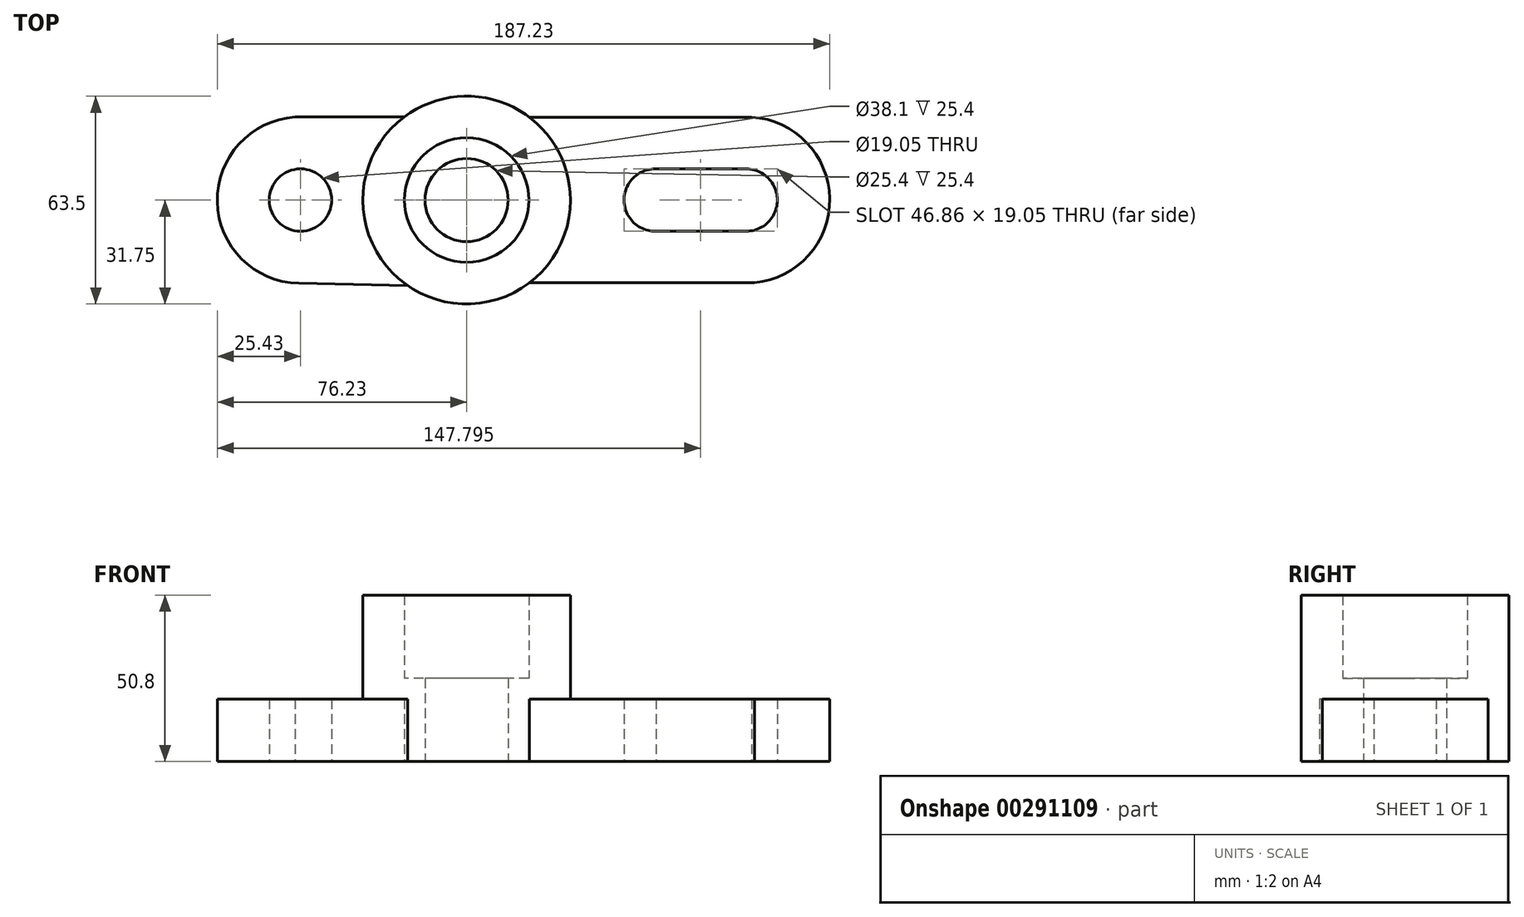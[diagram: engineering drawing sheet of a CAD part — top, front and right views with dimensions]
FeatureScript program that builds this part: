
annotation { "Feature Type Name" : "Feature", "Feature Type Description" : "" }
export const myFeature = defineFeature(function(context is Context, id is Id, definition is map)
    precondition{}
    {
        {
            var Q0;
            Q0=qCreatedBy(makeId("Top.planeOp"),FACE);
            var sketch = newSketch(context, id + "F0", { "sketchPlane" : qUnion([Q0])});
            skCircle(sketch, "E0", {"center": v(0, 0) * mm, "radius": 31.75 * mm});
            skCircle(sketch, "E1", {"center": v(0, 0) * mm, "radius": 19.05 * mm});
            skCircle(sketch, "E2", {"center": v(0, 0) * mm, "radius": 12.7 * mm});
            skPoint(sketch, "E3.center.orphan", {"position": v(85.6, 0) * mm});
            skArc(sketch, "E4", {"start": v(83.2, -25.29) * mm, "mid": v(111, -0.42) * mm, "end": v(84.04, 25.35) * mm});
            skPoint(sketch, "E5.center.orphan", {"position": v(-50.8, 0) * mm});
            skArc(sketch, "E6", {"start": v(-49.13, 25.37) * mm, "mid": v(-76.2, 1.12) * mm, "end": v(-51.37, -25.42) * mm});
            skLineSegment(sketch, "E7", {"start": v(87.16, 25.35) * mm, "end": v(19.11, 25.35) * mm});
            skLineSegment(sketch, "E8", {"start": v(88, -25.29) * mm, "end": v(19.2, -25.29) * mm});
            skLineSegment(sketch, "E9", {"start": v(-52.47, 25.37) * mm, "end": v(-19.08, 25.37) * mm});
            skLineSegment(sketch, "E10", {"start": v(-51.37, -25.42) * mm, "end": v(-17.98, -26.17) * mm});
            skArc(sketch, "E11", {"start": v(85.47, -9.52) * mm, "mid": v(95, 0) * mm, "end": v(85.47, 9.53) * mm});
            skArc(sketch, "E12", {"start": v(57.66, 9.52) * mm, "mid": v(48.13, -0.16) * mm, "end": v(57.97, -9.52) * mm});
            skLineSegment(sketch, "E13", {"start": v(57.66, 9.52) * mm, "end": v(85.47, 9.53) * mm});
            skLineSegment(sketch, "E14", {"start": v(57.97, -9.52) * mm, "end": v(85.47, -9.52) * mm});
            skCircle(sketch, "E15", {"center": v(-50.8, 0) * mm, "radius": 9.53 * mm});
            skSolve(sketch);
        }
        {
            var Q0;
            Q0=makeQuery(id+"F0.imprint","IMPRINT",FACE,{"disambiguationData":[TD([[makeQuery(id+"F0.imprint","IMPRINT",EDGE,{"derivedFrom":sQuery(id+"F0.wireOp",EDGE,"E1")}),-1.0]])]});
            extrude(context, id + "F1", {"entities" : qUnion([Q0]), "depth" : 50.8 * mm});
        }
        {
            var Q0;
            {var subQ4=sQuery(id+"F0.wireOp",EDGE,"E10");Q0=makeQuery(id+"F0.imprint","IMPRINT",FACE,{"disambiguationData":[TD([[makeQuery(id+"F0.imprint","IMPRINT",EDGE,{"derivedFrom":subQ4}),1.0]])]});}
            var Q1;
            Q1=makeQuery(id+"F0.imprint","IMPRINT",FACE,{"disambiguationData":[TD([[makeQuery(id+"F0.imprint","IMPRINT",EDGE,{"derivedFrom":sQuery(id+"F0.wireOp",EDGE,"E11")}),-1.0]])]});
            extrude(context, id + "F2", {"entities" : qUnion([Q0, Q1]), "operationType" : NewBodyOperationType.ADD, "depth" : 19.05 * mm});
        }
        {
            var Q0;
            Q0=makeQuery(id+"F0.imprint","IMPRINT",FACE,{"disambiguationData":[TD([[makeQuery(id+"F0.imprint","IMPRINT",EDGE,{"derivedFrom":sQuery(id+"F0.wireOp",EDGE,"E1")}),1.0]])]});
            extrude(context, id + "F3", {"entities" : qUnion([Q0]), "operationType" : NewBodyOperationType.ADD, "depth" : 25.4 * mm});
        }
    });
